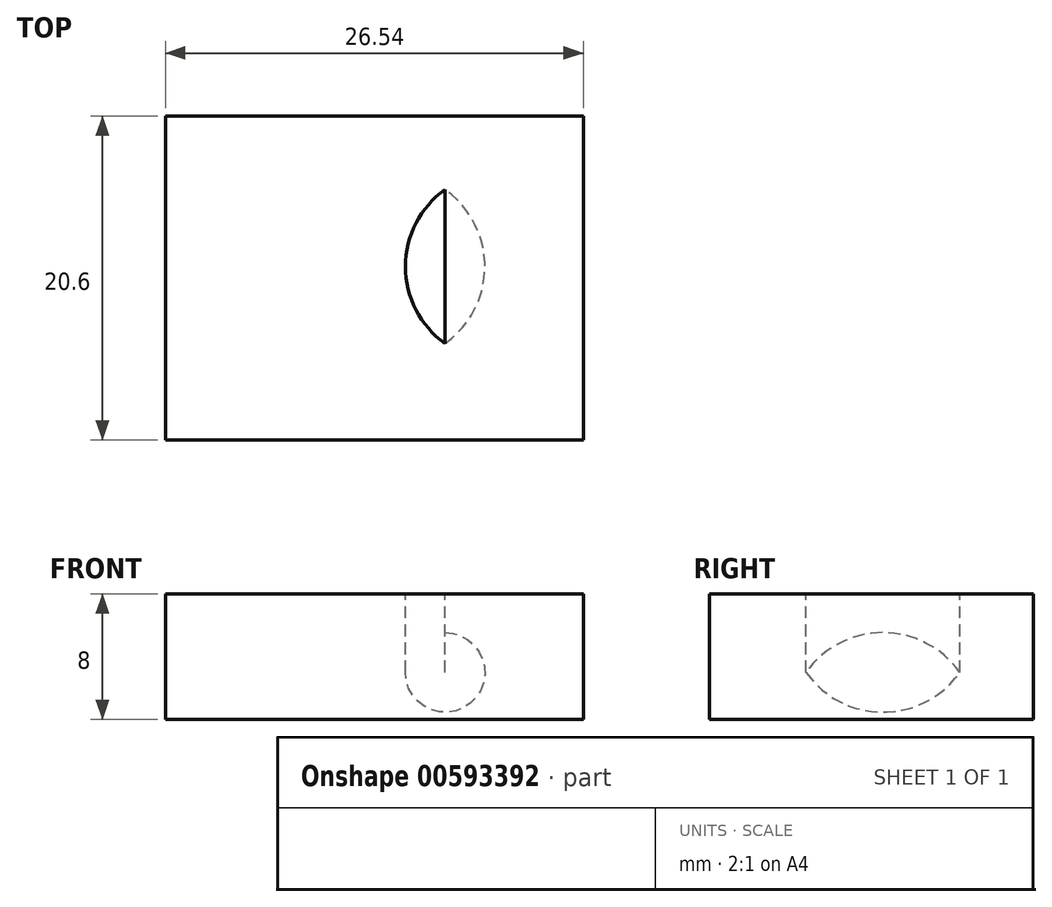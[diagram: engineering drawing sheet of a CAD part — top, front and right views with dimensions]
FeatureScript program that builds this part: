
annotation { "Feature Type Name" : "Feature", "Feature Type Description" : "" }
export const myFeature = defineFeature(function(context is Context, id is Id, definition is map)
    precondition{}
    {
        {
            var Q0;
            Q0=qCreatedBy(makeId("Top.planeOp"),FACE);
            var sketch = newSketch(context, id + "F0", { "sketchPlane" : qUnion([Q0])});
            skLineSegment(sketch, "E0.bottom", {"start": v(-12.28, 10.74) * mm, "end": v(14.26, 10.74) * mm});
            skLineSegment(sketch, "E0.top", {"start": v(-12.28, -9.86) * mm, "end": v(14.26, -9.86) * mm});
            skLineSegment(sketch, "E0.left", {"start": v(-12.28, 10.74) * mm, "end": v(-12.28, -9.86) * mm});
            skLineSegment(sketch, "E0.right", {"start": v(14.26, 10.74) * mm, "end": v(14.26, -9.86) * mm});
            skSolve(sketch);
        }
        {
            var Q0;
            Q0=makeQuery(id+"F0.imprint","IMPRINT",FACE,{"disambiguationData":[TD([[makeQuery(id+"F0.imprint","IMPRINT",EDGE,{"derivedFrom":sQuery(id+"F0.wireOp",EDGE,"E0.bottom")}),-1.0]])]});
            extrude(context, id + "F1", {"entities" : qUnion([Q0]), "depth" : 8 * mm, "offsetDistance" : 25 * mm});
        }
        {
            var Q0;
            Q0=makeQuery(id+"F1.opExtrude","CAP_FACE",FACE,{"disambiguationData":[OSD([sQuery(id+"F0.wireOp",EDGE,"E0.bottom"),sQuery(id+"F0.wireOp",EDGE,"E0.top"),sQuery(id+"F0.wireOp",EDGE,"E0.left"),sQuery(id+"F0.wireOp",EDGE,"E0.right")])],"isStart":false});
            var sketch = newSketch(context, id + "F2", { "sketchPlane" : qUnion([Q0])});
            skCircle(sketch, "E1", {"center": v(8.95, 1.17) * mm, "radius": 5.99 * mm});
            skLineSegment(sketch, "E2.bottom", {"start": v(-6.06, 6.05) * mm, "end": v(5.49, 6.05) * mm});
            skLineSegment(sketch, "E2.top", {"start": v(-6.06, -3.71) * mm, "end": v(5.49, -3.71) * mm});
            skLineSegment(sketch, "E2.left", {"start": v(-6.06, 6.05) * mm, "end": v(-6.06, -3.71) * mm});
            skLineSegment(sketch, "E2.right", {"start": v(5.49, 6.05) * mm, "end": v(5.49, -3.71) * mm});
            skSolve(sketch);
        }
        {
            var Q0;
            {var subQ0=sQuery(id+"F2.wireOp",EDGE,"E2.right");Q0=makeQuery(id+"F2.imprint","IMPRINT",FACE,{"disambiguationData":[TD([[makeQuery(id+"F2.imprint","IMPRINT",EDGE,{"derivedFrom":subQ0}),-1.0]])]});}
            extrude(context, id + "F3", {"entities" : qUnion([Q0]), "operationType" : NewBodyOperationType.REMOVE, "oppositeDirection" : true, "depth" : 5 * mm, "offsetDistance" : 25 * mm});
        }
        {
            var Q0;
            Q0=makeQuery(id+"F3.boolean.opBoolean","COPY",FACE,{"derivedFrom":makeQuery(id+"F3.opExtrude","CAP_FACE",FACE,{"disambiguationData":[OSD([sQuery(id+"F2.wireOp",EDGE,"E1"),sQuery(id+"F2.wireOp",EDGE,"E2.right")])],"isStart":false})});
            var Q1;
            Q1=makeQuery(id+"F3.boolean.opBoolean","COPY",EDGE,{"derivedFrom":makeQuery(id+"F3.opExtrude","CAP_EDGE",EDGE,{"disambiguationData":[OSD([sQuery(id+"F2.wireOp",EDGE,"E2.right")])],"isStart":false})});
            revolve(context, id + "F4", {"operationType" : NewBodyOperationType.REMOVE, "entities" : qUnion([Q0]), "axis" : qUnion([Q1]), "revolveType" : RevolveType.FULL});
        }
    });
